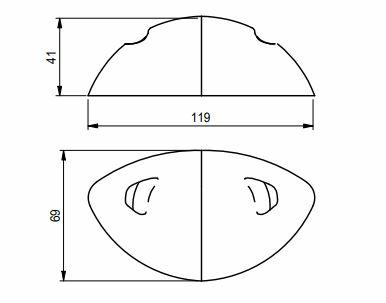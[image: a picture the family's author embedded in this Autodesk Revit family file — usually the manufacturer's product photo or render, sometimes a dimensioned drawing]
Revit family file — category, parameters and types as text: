
# Revit family: R-MBD-484
name_source: partatom
category: Portes
units: mm (PartAtom-declared; Revit-internal decimal feet)

## family parameters
Couper avec des vides une fois chargée = Non
Hôte = Mur
Partagée = Non
Repère de localisation dans la pièce = Oui
Toujours verticalement = Oui

## types (1)
- MBD-484
    1 Vantail = Oui
    2 Vantaux = Non
    A.E.V = non
    Acoustique = non
    Anti-Effraction = non
    Certification = D.A.S. Mode 2 certifié NF
    Code_MAJ = 2403130305MBD484
    Coloris_Chants = BER
    Coloris_Dormant = Hêtre
    Coloris_Face_Cote_Oppose_Ouverture = Prépeint
    Coloris_Face_Cote_Ouverture = Prépeint
    Construction analytique = <Aucun>
    DAS = Oui
    DC Larg Feuillure = 12 mm  [stored 0.0393701 ft]
    DC Pivot Vantail = 60 mm  [stored 0.19685 ft]
    Description = Bloc-porte bois D.A.S. 2 vantaux avec pivots linteaux motorisés encastrés, double action / va-et-vient, EI30, D.A.S. certifié NF, sur huisserie bois sans montant avec fileur
    Définir les propriétés thermiques par = Type schématique
    Ep Profil Pose Tunnel = 118 mm
    Ep Strat Vantail = 1 mm  [stored 0.00328084 ft]
    Ep Vantail = 46 mm  [stored 0.150919 ft]
    Epaisseur_Rainure à brique = 8 mm  [stored 0.0262467 ft]
    Fabricant = MALERBA
    Fiche_Produit = MBD-484
    Fileur = Oui
    Hauteur_Tableau = 2125 mm
    Hauteur_Vantaux_Souhaitée = 2040 mm  [stored 6.69291 ft]
    Jeu_1 = 0 mm  [stored 0 ft]
    Jeu_2 = 0 mm  [stored 0 ft]
    Jeu_Côté_Articulation_Vantail = 8 mm  [stored 0.0262467 ft]
    Jeu_Côté_Fermeture_Vantail = 8 mm  [stored 0.0262467 ft]
    Jeu_Haut = 3 mm  [stored 0.00984252 ft]
    Larg Profil = 58 mm  [stored 0.190289 ft]
    Larg Profil Avec Fileur = 20 mm  [stored 0.0656168 ft]
    Larg Profil Trav = 76 mm  [stored 0.249344 ft]
    Largeur = 0 mm  [stored 0 ft]
    Largeur_Vantail_Semi_Fixe_Souhaitée = 930 mm  [stored 3.05118 ft]
    Largeur_Vantail_Service_Souhaitée = 930 mm  [stored 3.05118 ft]
    Mat APD = Caoutchouc noir
    Mat Parclose = BER 2
    Mat Parclose Métal = Peinture Laquée PMT - Blanc Pur - RAL 9010
    Materiaux_Dominant = Bois
    Modèle = Va et vient
    Montant_VV = Non
    Note d'identification = 1V EI30 DAS - LINTEAU MOTORISE - SANS MONTANT SANS FILEUR
    Pivot linteau motorisé = Oui
    Profondeur_Rainure à brique = 5 mm  [stored 0.0164042 ft]
    Reference_Commerciale = 1V/DA LINTEAU OP
    Resistance_Feu = EI30
    Sans_Montants = Non
    Sens_Feu = Recto / Verso
    Thermique (W/m2.°K) = 0
    URL = https://www.malerba.fr
    X_Axe Pivot = 88 mm  [stored 0.288714 ft]
    X_DC seuil = 9 mm  [stored 0.0295276 ft]
    X_Inv_DC Larg Feuillure_1V Montant = 0 mm  [stored 0 ft]

note: [stored X ft] marks values corroborated as IEEE doubles in the binary element streams (Revit-internal decimal feet)

## geometry (parser evidence)
native form markers: Blend x14
no freeform markers — native parametric forms only
